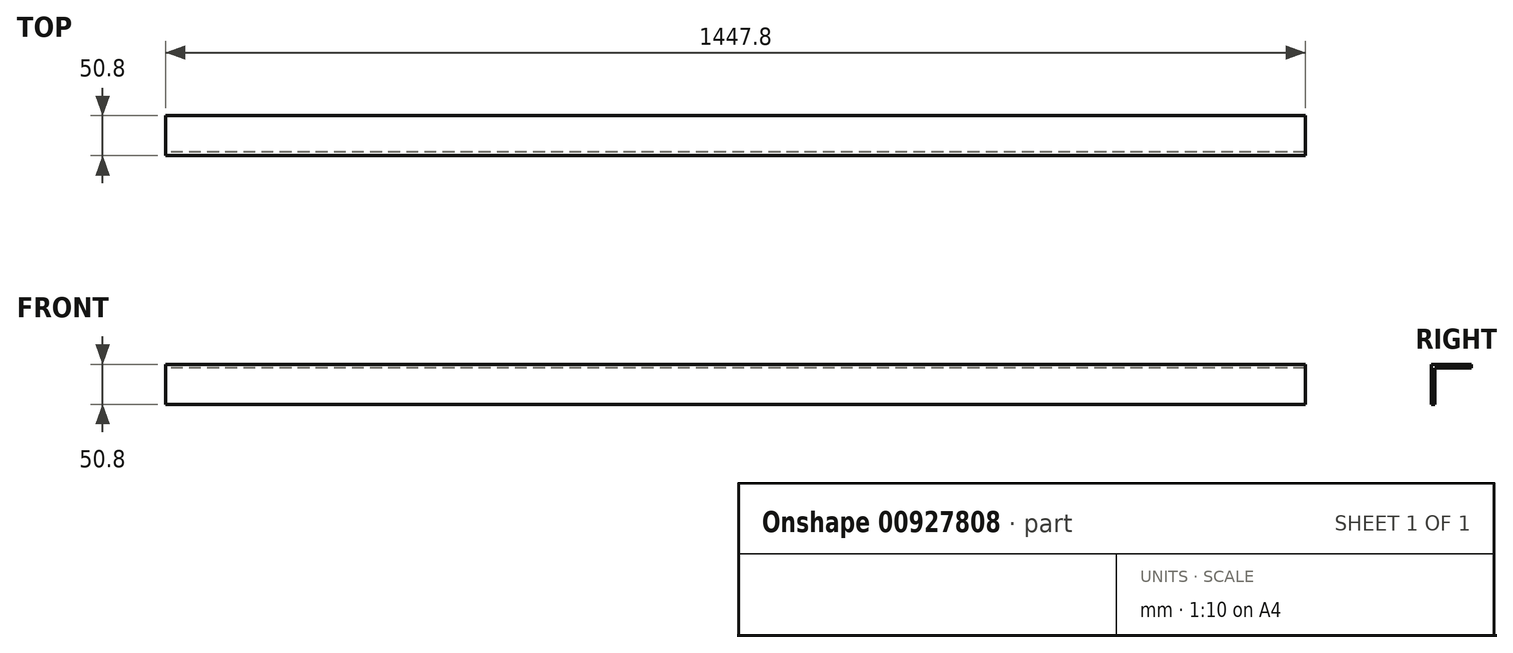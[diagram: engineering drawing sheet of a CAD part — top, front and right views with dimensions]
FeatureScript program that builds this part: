
annotation { "Feature Type Name" : "Feature", "Feature Type Description" : "" }
export const myFeature = defineFeature(function(context is Context, id is Id, definition is map)
    precondition{}
    {
        {
            var Q0;
            Q0=qCreatedBy(makeId("Right.planeOp"),FACE);
            var sketch = newSketch(context, id + "F0", { "sketchPlane" : qUnion([Q0])});
            skLineSegment(sketch, "E0", {"start": v(0, -29.22) * mm, "end": v(0, 21.58) * mm});
            skLineSegment(sketch, "E1", {"start": v(0, 21.58) * mm, "end": v(50.8, 21.58) * mm});
            skLineSegment(sketch, "E2", {"start": v(50.8, 21.58) * mm, "end": v(50.8, 17.14) * mm});
            skLineSegment(sketch, "E3", {"start": v(50.8, 17.14) * mm, "end": v(0, 17.14) * mm});
            skLineSegment(sketch, "E4", {"start": v(0, -29.22) * mm, "end": v(4.44, -29.22) * mm});
            skLineSegment(sketch, "E5", {"start": v(4.44, -29.22) * mm, "end": v(4.44, 21.58) * mm});
            skSolve(sketch);
        }
        {
            var Q0;
            Q0 = qSketchRegion(id + "F0", true);
            extrude(context, id + "F1", {"entities" : qUnion([Q0]), "depth" : 1447.8 * mm, "offsetDistance" : 25.4 * mm});
        }
    });
